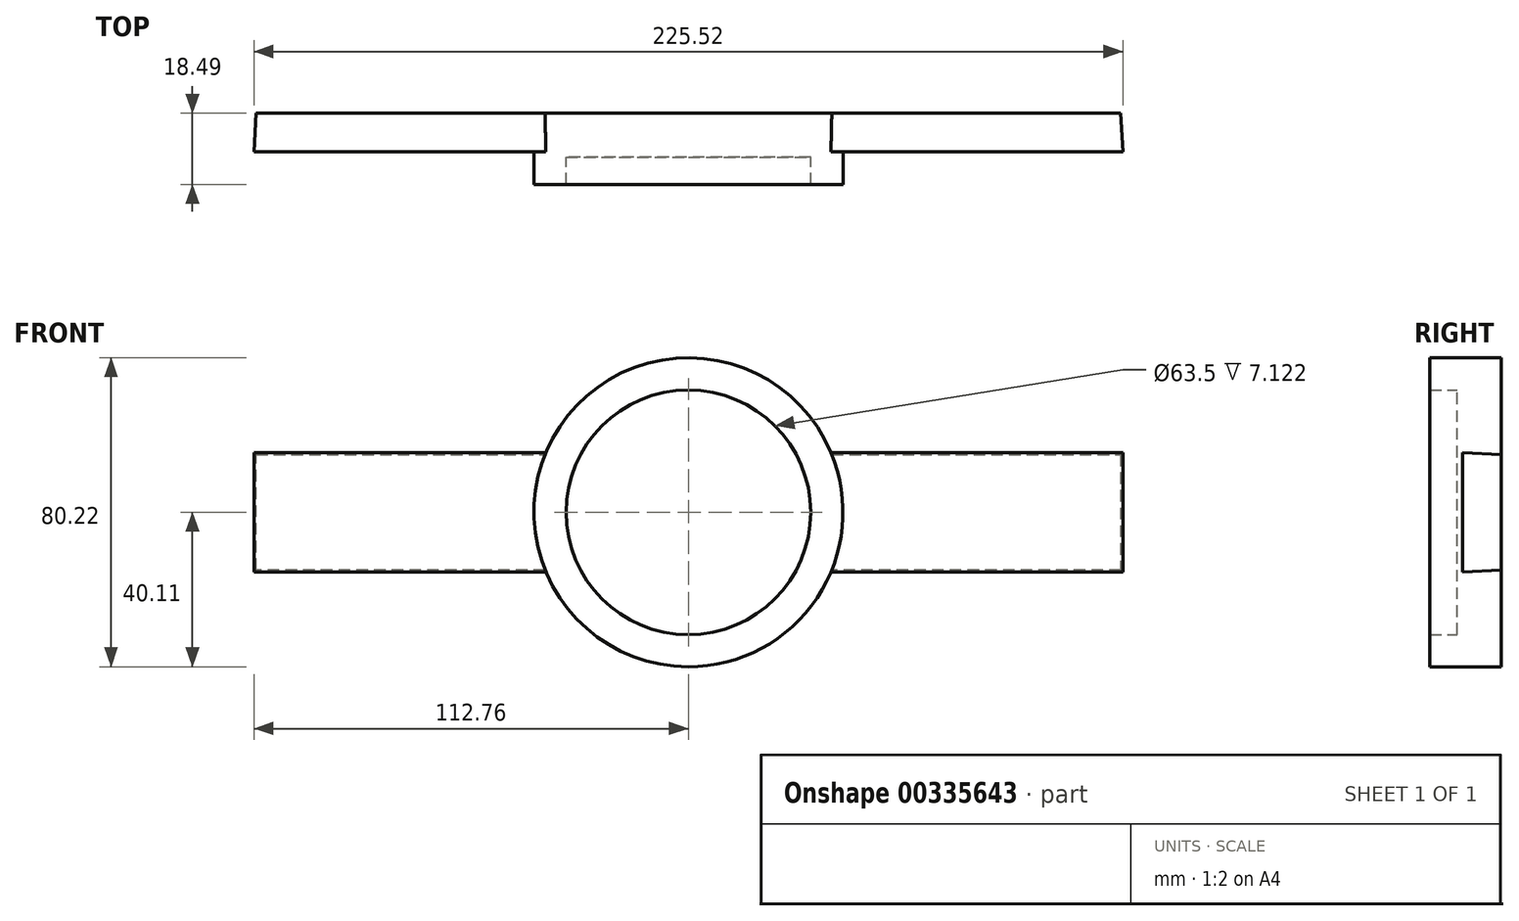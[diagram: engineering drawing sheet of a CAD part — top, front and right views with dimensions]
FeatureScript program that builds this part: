
annotation { "Feature Type Name" : "Feature", "Feature Type Description" : "" }
export const myFeature = defineFeature(function(context is Context, id is Id, definition is map)
    precondition{}
    {
        {
            var Q0;
            Q0=qCreatedBy(makeId("Front.planeOp"),FACE);
            var sketch = newSketch(context, id + "F0", { "sketchPlane" : qUnion([Q0])});
            skCircle(sketch, "E0", {"center": v(0, 0) * mm, "radius": 32.7 * mm});
            skSolve(sketch);
        }
        {
            var Q0;
            Q0 = qSketchRegion(id + "F0", true);
            extrude(context, id + "F1", {"entities" : qUnion([Q0]), "depth" : 14.65 * mm});
        }
        {
            var Q0;
            Q0=qCreatedBy(makeId("Front.planeOp"),FACE);
            var sketch = newSketch(context, id + "F2", { "sketchPlane" : qUnion([Q0])});
            skLineSegment(sketch, "E1.bottom", {"start": v(112.24, 14.98) * mm, "end": v(-112.24, 14.98) * mm});
            skLineSegment(sketch, "E1.top", {"start": v(112.24, -14.98) * mm, "end": v(-112.24, -14.98) * mm});
            skLineSegment(sketch, "E1.left", {"start": v(112.24, 14.98) * mm, "end": v(112.24, -14.98) * mm});
            skLineSegment(sketch, "E1.right", {"start": v(-112.24, 14.98) * mm, "end": v(-112.24, -14.98) * mm});
            skPoint(sketch, "E1.middle", {"position": v(0, 0) * mm});
            skSolve(sketch);
        }
        {
            var Q0;
            Q0=makeQuery(id+"F2.imprint","IMPRINT",FACE,{"disambiguationData":[TD([[makeQuery(id+"F2.imprint","IMPRINT",EDGE,{"derivedFrom":sQuery(id+"F2.wireOp",EDGE,"E1.bottom")}),1.0]])]});
            extrude(context, id + "F3", {"entities" : qUnion([Q0]), "operationType" : NewBodyOperationType.ADD, "depth" : 10.03 * mm, "hasDraft" : true, "draftAngle" : 3 * degree});
        }
        {
            var Q0;
            Q0=qCreatedBy(makeId("Front.planeOp"),FACE);
            var sketch = newSketch(context, id + "F4", { "sketchPlane" : qUnion([Q0])});
            skCircle(sketch, "E2", {"center": v(0, 0) * mm, "radius": 40.11 * mm});
            skSolve(sketch);
        }
        {
            var Q0;
            Q0 = qSketchRegion(id + "F4", true);
            extrude(context, id + "F5", {"entities" : qUnion([Q0]), "operationType" : NewBodyOperationType.ADD, "depth" : 18.5 * mm});
        }
        {
            var Q0;
            Q0 = qSketchRegion(id + "F0", true);
            var sketch = newSketch(context, id + "F6", { "sketchPlane" : qUnion([Q0])});
            skCircle(sketch, "E3", {"center": v(0, 0) * mm, "radius": 32.71 * mm});
            skSolve(sketch);
        }
        {
            var Q0;
            Q0=sQuery(id+"F0.wireOp",VERTEX,"E0.center");
            var Q1;
            Q1=makeQuery(id+"F1.opExtrude","SWEPT_BODY",BODY,{"disambiguationData":[OSD([sQuery(id+"F0.wireOp",EDGE,"E0")])]});
            hole(context, id + "F7", {"style" : HoleStyle.SIMPLE, "endStyle" : HoleEndStyle.BLIND, "oppositeDirection" : true, "holeDiameter" : 63.5 * mm, "holeDepth" : 50.8 * mm, "tappedDepth" : 12.7 * mm, "tapClearance" : 3, "locations" : qUnion([Q0]), "scope" : qUnion([Q1])});
        }
        {
            var Q0;
            Q0=makeQuery(id+"F0.imprint","IMPRINT",FACE,{"disambiguationData":[TD([[makeQuery(id+"F0.imprint","IMPRINT",EDGE,{"derivedFrom":sQuery(id+"F0.wireOp",EDGE,"E0")}),1.0]])]});
            extrude(context, id + "F8", {"entities" : qUnion([Q0]), "operationType" : NewBodyOperationType.ADD, "depth" : 11.37 * mm});
        }
    });
